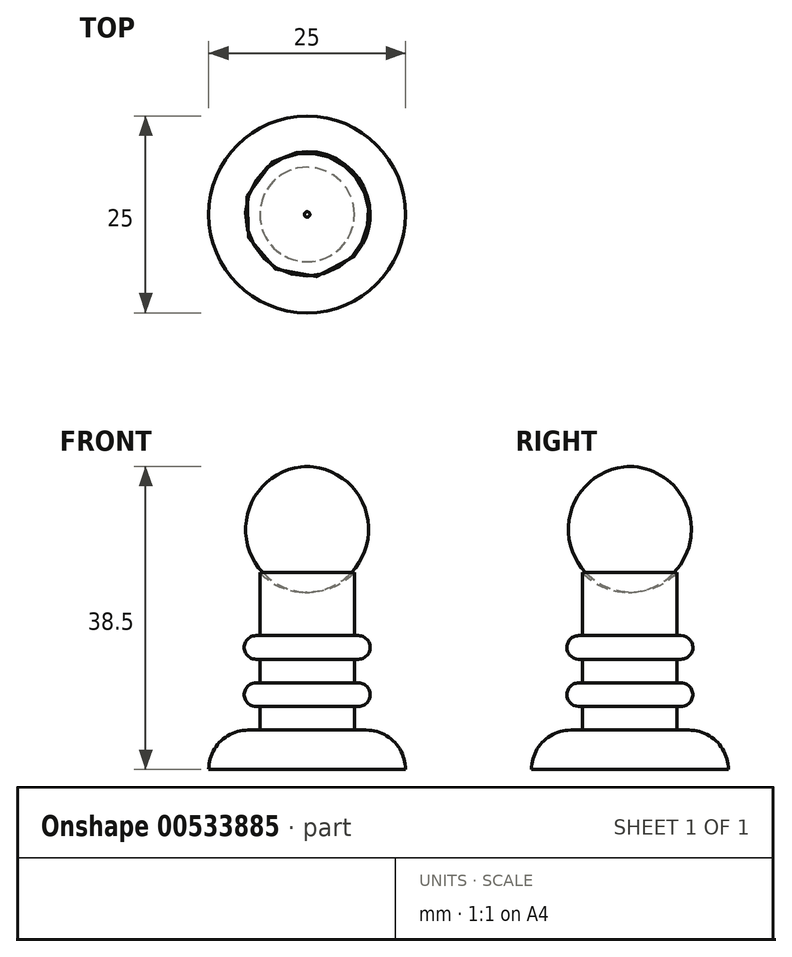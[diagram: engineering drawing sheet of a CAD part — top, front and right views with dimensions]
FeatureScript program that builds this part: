
annotation { "Feature Type Name" : "Feature", "Feature Type Description" : "" }
export const myFeature = defineFeature(function(context is Context, id is Id, definition is map)
    precondition{}
    {
        {
            assignVariable(context, id + "F0", {"name" : "base_height", "anyValue" : 5});
        }
        {
            assignVariable(context, id + "F1", {"name" : "tower_height", "anyValue" : 25});
        }
        {
            assignVariable(context, id + "F2", {"name" : "ring_height", "anyValue" : 3});
        }
        {
            var Q0;
            Q0=qCreatedBy(makeId("Top.planeOp"),FACE);
            var sketch = newSketch(context, id + "F3", { "sketchPlane" : qUnion([Q0])});
            skCircle(sketch, "E0", {"center": v(0, 0) * mm, "radius": 12.5 * mm});
            skCircle(sketch, "E1", {"center": v(0, 0) * mm, "radius": 6 * mm});
            skCircle(sketch, "E2.0", {"center": v(0, 0) * mm, "radius": 8 * mm});
            skSolve(sketch);
        }
        {
            var Q0;
            Q0=makeQuery(id+"F3.imprint","IMPRINT",FACE,{"disambiguationData":[TD([[makeQuery(id+"F3.imprint","IMPRINT",EDGE,{"derivedFrom":sQuery(id+"F3.wireOp",EDGE,"E0")}),1.0]])]});
            var Q1;
            Q1=makeQuery(id+"F3.imprint","IMPRINT",FACE,{"disambiguationData":[TD([[makeQuery(id+"F3.imprint","IMPRINT",EDGE,{"derivedFrom":sQuery(id+"F3.wireOp",EDGE,"E1")}),-1.0]])]});
            var Q2;
            Q2=makeQuery(id+"F3.imprint","IMPRINT",FACE,{"disambiguationData":[TD([[makeQuery(id+"F3.imprint","IMPRINT",EDGE,{"derivedFrom":sQuery(id+"F3.wireOp",EDGE,"E1")}),1.0]])]});
            extrude(context, id + "F4", {"entities" : qUnion([Q0, Q1, Q2]), "depth" : getVariable(context, 'base_height') * mm, "offsetDistance" : 25 * mm});
        }
        {
            var Q0;
            Q0=makeQuery(id+"F3.imprint","IMPRINT",FACE,{"disambiguationData":[TD([[makeQuery(id+"F3.imprint","IMPRINT",EDGE,{"derivedFrom":sQuery(id+"F3.wireOp",EDGE,"E1")}),1.0]])]});
            extrude(context, id + "F5", {"entities" : qUnion([Q0]), "operationType" : NewBodyOperationType.ADD, "depth" : (getVariable(context, 'tower_height')) * mm, "offsetDistance" : 25 * mm});
        }
        {
            var Q0;
            Q0=makeQuery(id+"F3.imprint","IMPRINT",FACE,{"disambiguationData":[TD([[makeQuery(id+"F3.imprint","IMPRINT",EDGE,{"derivedFrom":sQuery(id+"F3.wireOp",EDGE,"E1")}),-1.0]])]});
            extrude(context, id + "F6", {"entities" : qUnion([Q0]), "operationType" : NewBodyOperationType.ADD, "depth" : (getVariable(context, 'base_height') + getVariable(context, 'ring_height') * 2) * mm, "offsetDistance" : 25 * mm, "hasSecondDirection" : true, "secondDirectionOppositeDirection" : false, "secondDirectionDepth" : (getVariable(context, 'base_height') + getVariable(context, 'ring_height')) * mm});
        }
        {
            var Q0;
            Q0=makeQuery(id+"F3.imprint","IMPRINT",FACE,{"disambiguationData":[TD([[makeQuery(id+"F3.imprint","IMPRINT",EDGE,{"derivedFrom":sQuery(id+"F3.wireOp",EDGE,"E1")}),-1.0]])]});
            extrude(context, id + "F7", {"entities" : qUnion([Q0]), "operationType" : NewBodyOperationType.ADD, "depth" : (getVariable(context, 'base_height') + getVariable(context, 'ring_height') * 4) * mm, "offsetDistance" : 25 * mm, "hasSecondDirection" : true, "secondDirectionOppositeDirection" : false, "secondDirectionDepth" : (getVariable(context, 'base_height') + getVariable(context, 'ring_height') * 3) * mm});
        }
        {
            var Q0;
            Q0=makeQuery(id+"F6.opExtrude","CAP_EDGE",EDGE,{"disambiguationData":[OSD([sQuery(id+"F3.wireOp",EDGE,"E2.0")])],"isStart":true});
            var Q1;
            Q1=makeQuery(id+"F6.opExtrude","CAP_EDGE",EDGE,{"disambiguationData":[OSD([sQuery(id+"F3.wireOp",EDGE,"E2.0")])],"isStart":false});
            fillet(context, id + "F8", {"entities" : qUnion([Q0, Q1]), "radius" : 1.5 * mm, "tangentPropagation" : true, "allowEdgeOverflow" : false});
        }
        {
            var Q0;
            Q0=makeQuery(id+"F7.opExtrude","CAP_EDGE",EDGE,{"disambiguationData":[OSD([sQuery(id+"F3.wireOp",EDGE,"E2.0")])],"isStart":true});
            var Q1;
            Q1=makeQuery(id+"F7.opExtrude","CAP_EDGE",EDGE,{"disambiguationData":[OSD([sQuery(id+"F3.wireOp",EDGE,"E2.0")])],"isStart":false});
            fillet(context, id + "F9", {"entities" : qUnion([Q0, Q1]), "radius" : 1.5 * mm, "tangentPropagation" : true, "allowEdgeOverflow" : false});
        }
        {
            var Q0;
            Q0=makeQuery(id+"F4.opExtrude","CAP_EDGE",EDGE,{"disambiguationData":[OSD([sQuery(id+"F3.wireOp",EDGE,"E0")])],"isStart":false});
            fillet(context, id + "F10", {"entities" : qUnion([Q0]), "radius" : (getVariable(context, 'base_height')) * mm, "tangentPropagation" : true, "allowEdgeOverflow" : false});
        }
        {
            assignVariable(context, id + "F11", {"name" : "crown_dia", "anyValue" : 18});
        }
        {
            var Q0;
            Q0=qCreatedBy(makeId("Top.planeOp"),FACE);
            var sketch = newSketch(context, id + "F12", { "sketchPlane" : qUnion([Q0])});
            skCircle(sketch, "E3", {"center": v(0, 0) * mm, "radius": 9 * mm});
            skSolve(sketch);
        }
        {
            var Q0;
            Q0=makeQuery(id+"F12.imprint","IMPRINT",FACE,{"disambiguationData":[TD([[makeQuery(id+"F12.imprint","IMPRINT",EDGE,{"derivedFrom":sQuery(id+"F12.wireOp",EDGE,"E3")}),1.0]])]});
            extrude(context, id + "F13", {"entities" : qUnion([Q0]), "operationType" : NewBodyOperationType.ADD, "depth" : (getVariable(context, 'tower_height') + getVariable(context, 'crown_dia') * .75) * mm, "offsetDistance" : 25 * mm, "hasSecondDirection" : true, "secondDirectionOppositeDirection" : false, "secondDirectionDepth" : (getVariable(context, 'tower_height')) * mm});
        }
        {
            var Q0;
            Q0=makeQuery(id+"F13.opExtrude","CAP_EDGE",EDGE,{"disambiguationData":[OSD([sQuery(id+"F12.wireOp",EDGE,"E3")])],"isStart":true});
            fillet(context, id + "F14", {"entities" : qUnion([Q0]), "radius" : (getVariable(context, 'crown_dia') / 2 - 1) * mm, "tangentPropagation" : true, "allowEdgeOverflow" : false});
        }
        {
            var Q0;
            Q0=makeQuery(id+"F13.opExtrude","CAP_EDGE",EDGE,{"disambiguationData":[OSD([sQuery(id+"F12.wireOp",EDGE,"E3")])],"isStart":false});
            fillet(context, id + "F15", {"entities" : qUnion([Q0]), "radius" : (getVariable(context, 'crown_dia') / 2) * mm, "tangentPropagation" : true, "allowEdgeOverflow" : false});
        }
        {
            var Q0;
            {var subQ0=sQuery(id+"F12.wireOp",EDGE,"E3");Q0=makeQuery(id+"F15.opFillet","BLEND_EDGE",EDGE,{"blendedFrom":[makeQuery(id+"F13.opExtrude","CAP_EDGE",EDGE,{"disambiguationData":[OSD([subQ0])],"isStart":false}),makeQuery(id+"F14.opFillet","BLEND_FACE",FACE,{"disambiguationData":[OSD([subQ0])]})],"blendedInto":[makeQuery(id+"F14.opFillet","BLEND_FACE",FACE,{"disambiguationData":[OSD([subQ0])]})]});}
            fillet(context, id + "F16", {"entities" : qUnion([Q0]), "radius" : 8 * mm, "tangentPropagation" : true, "allowEdgeOverflow" : false});
        }
    });
